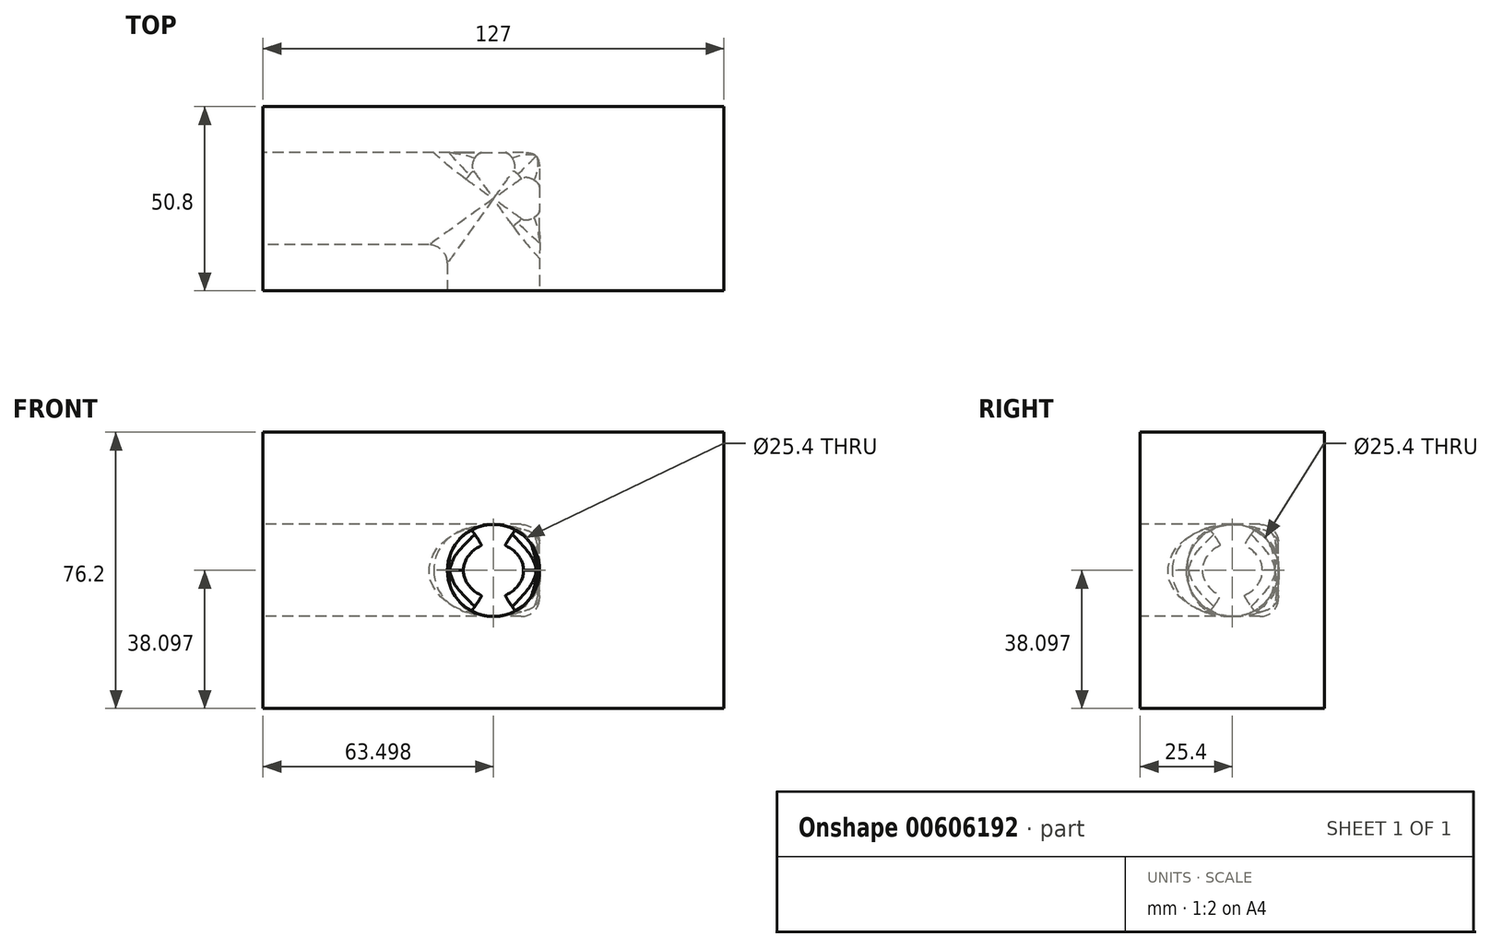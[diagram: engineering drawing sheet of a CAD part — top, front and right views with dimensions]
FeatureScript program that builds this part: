
annotation { "Feature Type Name" : "Feature", "Feature Type Description" : "" }
export const myFeature = defineFeature(function(context is Context, id is Id, definition is map)
    precondition{}
    {
        {
            var Q0;
            Q0=qCreatedBy(makeId("Front.planeOp"),FACE);
            var sketch = newSketch(context, id + "F0", { "sketchPlane" : qUnion([Q0])});
            skLineSegment(sketch, "E0.bottom", {"start": v(-31.91, 47.65) * mm, "end": v(95.09, 47.65) * mm});
            skLineSegment(sketch, "E0.top", {"start": v(-31.91, -28.55) * mm, "end": v(95.09, -28.55) * mm});
            skLineSegment(sketch, "E0.left", {"start": v(-31.91, 47.65) * mm, "end": v(-31.91, -28.55) * mm});
            skLineSegment(sketch, "E0.right", {"start": v(95.09, 47.65) * mm, "end": v(95.09, -28.55) * mm});
            skSolve(sketch);
        }
        {
            var Q0;
            Q0 = qSketchRegion(id + "F0", true);
            extrude(context, id + "F1", {"entities" : qUnion([Q0]), "depth" : 50.8 * mm, "offsetDistance" : 25.4 * mm});
        }
        {
            var Q0;
            Q0=makeQuery(id+"F1.opExtrude","CAP_FACE",FACE,{"disambiguationData":[OSD([sQuery(id+"F0.wireOp",EDGE,"E0.bottom"),sQuery(id+"F0.wireOp",EDGE,"E0.top"),sQuery(id+"F0.wireOp",EDGE,"E0.left"),sQuery(id+"F0.wireOp",EDGE,"E0.right")])],"isStart":false});
            var sketch = newSketch(context, id + "F2", { "sketchPlane" : qUnion([Q0])});
            skCircle(sketch, "E1", {"center": v(31.59, 9.55) * mm, "radius": 12.7 * mm});
            skSolve(sketch);
        }
        {
            var Q0;
            Q0=makeQuery(id+"F2.imprint","IMPRINT",FACE,{"disambiguationData":[TD([[makeQuery(id+"F2.imprint","IMPRINT",EDGE,{"derivedFrom":sQuery(id+"F2.wireOp",EDGE,"E1")}),1.0]])]});
            extrude(context, id + "F3", {"entities" : qUnion([Q0]), "operationType" : NewBodyOperationType.REMOVE, "oppositeDirection" : true, "depth" : 38.1 * mm, "offsetDistance" : 25.4 * mm});
        }
        {
            var Q0;
            Q0=makeQuery(id+"F1.opExtrude","SWEPT_FACE",FACE,{"disambiguationData":[OSD([sQuery(id+"F0.wireOp",EDGE,"E0.left")])]});
            var sketch = newSketch(context, id + "F4", { "sketchPlane" : qUnion([Q0])});
            skCircle(sketch, "E2", {"center": v(25.4, 9.55) * mm, "radius": 12.7 * mm});
            skSolve(sketch);
        }
        {
            var Q0;
            Q0=makeQuery(id+"F4.imprint","IMPRINT",FACE,{"disambiguationData":[TD([[makeQuery(id+"F4.imprint","IMPRINT",EDGE,{"derivedFrom":sQuery(id+"F4.wireOp",EDGE,"E2")}),1.0]])]});
            extrude(context, id + "F5", {"entities" : qUnion([Q0]), "operationType" : NewBodyOperationType.REMOVE, "oppositeDirection" : true, "depth" : 76.2 * mm, "offsetDistance" : 25.4 * mm});
        }
        {
            var Q0;
            Q0=makeQuery(id+"F5.boolean.opBoolean","INTERSECT",EDGE,{"disambiguationData":[OD(1.0)],"derivedFrom":[makeQuery(id+"F3.boolean.opBoolean","COPY",FACE,{"derivedFrom":makeQuery(id+"F3.opExtrude","SWEPT_FACE",FACE,{"disambiguationData":[OSD([sQuery(id+"F2.wireOp",EDGE,"E1")])]})}),makeQuery(id+"F5.opExtrude","SWEPT_FACE",FACE,{"disambiguationData":[OSD([sQuery(id+"F4.wireOp",EDGE,"E2")])]})]});
            var Q1;
            Q1=makeQuery(id+"F5.boolean.opBoolean","INTERSECT",EDGE,{"disambiguationData":[OD(5.0)],"derivedFrom":[makeQuery(id+"F3.boolean.opBoolean","COPY",FACE,{"derivedFrom":makeQuery(id+"F3.opExtrude","SWEPT_FACE",FACE,{"disambiguationData":[OSD([sQuery(id+"F2.wireOp",EDGE,"E1")])]})}),makeQuery(id+"F5.opExtrude","SWEPT_FACE",FACE,{"disambiguationData":[OSD([sQuery(id+"F4.wireOp",EDGE,"E2")])]})]});
            var Q2;
            Q2=makeQuery(id+"F5.boolean.opBoolean","INTERSECT",EDGE,{"disambiguationData":[OD(3.0)],"derivedFrom":[makeQuery(id+"F3.boolean.opBoolean","COPY",FACE,{"derivedFrom":makeQuery(id+"F3.opExtrude","SWEPT_FACE",FACE,{"disambiguationData":[OSD([sQuery(id+"F2.wireOp",EDGE,"E1")])]})}),makeQuery(id+"F5.opExtrude","SWEPT_FACE",FACE,{"disambiguationData":[OSD([sQuery(id+"F4.wireOp",EDGE,"E2")])]})]});
            var Q3;
            Q3=makeQuery(id+"F5.boolean.opBoolean","INTERSECT",EDGE,{"disambiguationData":[OD(0.0)],"derivedFrom":[makeQuery(id+"F3.boolean.opBoolean","COPY",FACE,{"derivedFrom":makeQuery(id+"F3.opExtrude","SWEPT_FACE",FACE,{"disambiguationData":[OSD([sQuery(id+"F2.wireOp",EDGE,"E1")])]})}),makeQuery(id+"F5.opExtrude","SWEPT_FACE",FACE,{"disambiguationData":[OSD([sQuery(id+"F4.wireOp",EDGE,"E2")])]})]});
            var Q4;
            Q4=makeQuery(id+"F5.boolean.opBoolean","SPLIT",EDGE,{"disambiguationData":[OD(0.0)],"derivedFrom":makeQuery(id+"F3.boolean.opBoolean","COPY",EDGE,{"derivedFrom":makeQuery(id+"F3.opExtrude","CAP_EDGE",EDGE,{"disambiguationData":[OSD([sQuery(id+"F2.wireOp",EDGE,"E1")])],"isStart":false})})});
            var Q5;
            {var subQ0=sQuery(id+"F2.wireOp",EDGE,"E1");var subQ1=sQuery(id+"F4.wireOp",EDGE,"E2");var subQ2=makeQuery(id+"F5.opExtrude","SWEPT_FACE",FACE,{"disambiguationData":[OSD([subQ1])]});Q5=makeQuery(id+"F5.boolean.opBoolean","COPY",FACE,{"disambiguationData":[TD([makeQuery(id+"F3.boolean.opBoolean","COPY",FACE,{"derivedFrom":makeQuery(id+"F3.opExtrude","SWEPT_FACE",FACE,{"disambiguationData":[OSD([subQ0])]})}),makeQuery(id+"F3.boolean.opBoolean","COPY",FACE,{"derivedFrom":makeQuery(id+"F3.opExtrude","CAP_FACE",FACE,{"disambiguationData":[OSD([subQ0])],"isStart":false})}),subQ2,makeQuery(id+"F5.opExtrude","CAP_FACE",FACE,{"disambiguationData":[OSD([subQ1])],"isStart":false})]),OD(0.0)],"derivedFrom":subQ2});}
            var Q6;
            Q6=makeQuery(id+"F5.boolean.opBoolean","INTERSECT",EDGE,{"disambiguationData":[OD(4.0)],"derivedFrom":[makeQuery(id+"F3.boolean.opBoolean","COPY",FACE,{"derivedFrom":makeQuery(id+"F3.opExtrude","SWEPT_FACE",FACE,{"disambiguationData":[OSD([sQuery(id+"F2.wireOp",EDGE,"E1")])]})}),makeQuery(id+"F5.opExtrude","SWEPT_FACE",FACE,{"disambiguationData":[OSD([sQuery(id+"F4.wireOp",EDGE,"E2")])]})]});
            var Q7;
            Q7=makeQuery(id+"F5.boolean.opBoolean","INTERSECT",EDGE,{"disambiguationData":[OD(6.0)],"derivedFrom":[makeQuery(id+"F3.boolean.opBoolean","COPY",FACE,{"derivedFrom":makeQuery(id+"F3.opExtrude","SWEPT_FACE",FACE,{"disambiguationData":[OSD([sQuery(id+"F2.wireOp",EDGE,"E1")])]})}),makeQuery(id+"F5.opExtrude","SWEPT_FACE",FACE,{"disambiguationData":[OSD([sQuery(id+"F4.wireOp",EDGE,"E2")])]})]});
            var Q8;
            Q8=makeQuery(id+"F5.boolean.opBoolean","COPY",EDGE,{"disambiguationData":[OD(1.0)],"derivedFrom":makeQuery(id+"F5.opExtrude","CAP_EDGE",EDGE,{"disambiguationData":[OSD([sQuery(id+"F4.wireOp",EDGE,"E2")])],"isStart":false})});
            fillet(context, id + "F6", {"entities" : qUnion([Q0, Q1, Q2, Q3, Q4, Q5, Q6, Q7, Q8]), "radius" : 5.08 * mm, "tangentPropagation" : true, "allowEdgeOverflow" : false});
        }
    });
